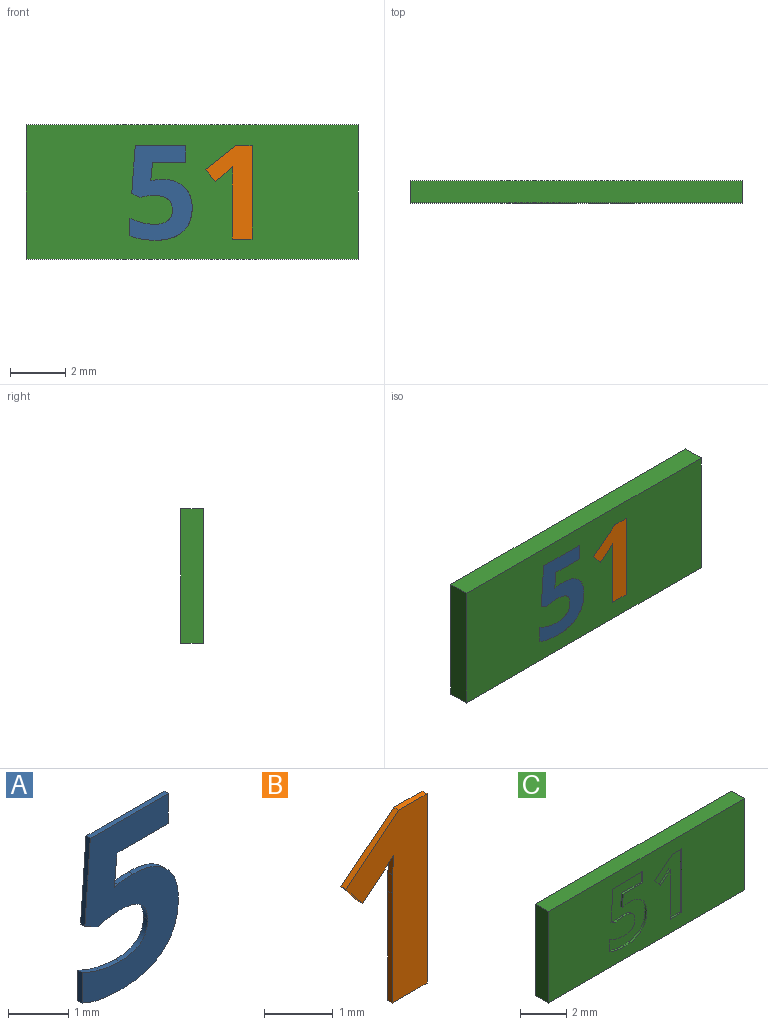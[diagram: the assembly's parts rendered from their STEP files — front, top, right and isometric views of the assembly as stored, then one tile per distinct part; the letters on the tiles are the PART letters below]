
ASSEMBLY  parts=3 mates=2
PART A: 22 faces, bbox 2.3x0.1x3.4 mm
  f0: plane 3.42x2.25mm, normal (0,-1,0), area 4.5mm2, adj f1,f2,f3,f4,f5,f6,f7,f8
  f1: plane 0.1x0.08mm, normal (-0.2,0,0.98), area 0mm2, adj f0,f2,f18,f20
  f2: plane 0.66x0.1mm, normal (1,0,-0.09), area 0.1mm2, adj f0,f1,f3,f18
  f3: plane 1.2x0.1mm, normal (0,0,-1), area 0.1mm2, adj f0,f2,f4,f18
  f4: plane 0.6x0.1mm, normal (1,0,0), area 0.1mm2, adj f0,f3,f5,f18
  f5: plane 1.83x0.1mm, normal (0,0,1), area 0.2mm2, adj f0,f4,f6,f18
  f6: plane 1.72x0.13mm, normal (-1,0,0.07), area 0.2mm2, adj f0,f5,f7,f18
  f7: plane 0.28x0.15mm, normal (-0.47,0,-0.88), area 0mm2, adj f0,f6,f8,f18
  f8: extruded ~0.24x0.1mm, area 0mm2, adj f0,f7,f9,f18
  f9: extruded ~0.27x0.1mm, area 0mm2, adj f0,f8,f10,f18
  f10: extruded ~0.68x0.51mm, area 0.1mm2, adj f0,f9,f11,f18
  f11: extruded ~0.65x0.54mm, area 0.1mm2, adj f0,f10,f12,f18
  f12: extruded ~0.46x0.1mm, area 0mm2, adj f0,f11,f13,f18
  f13: extruded ~0.42x0.16mm, area 0mm2, adj f0,f12,f14,f18
  f14: plane 0.62x0.1mm, normal (-1,0,0), area 0.1mm2, adj f0,f13,f15,f18
  f15: extruded ~0.91x0.18mm, area 0.1mm2, adj f0,f14,f16,f18
  f16: extruded ~1x0.3mm, area 0.1mm2, adj f0,f15,f17,f18
  f17: extruded ~0.87x0.35mm, area 0.1mm2, adj f0,f16,f18,f19
  f18: plane 3.42x2.25mm, normal (0,1,0), area 4.5mm2, adj f1,f2,f3,f4,f5,f6,f7,f8
  f19: extruded ~0.75x0.29mm, area 0.1mm2, adj f0,f17,f18,f21
  f20: extruded ~0.35x0.1mm, area 0mm2, adj f0,f1,f18,f21
  f21: extruded ~0.78x0.27mm, area 0.1mm2, adj f0,f18,f19,f20
PART B: 12 faces, bbox 1.7x0.1x3.4 mm
  f0: plane 3.37x1.67mm, normal (0,-1,0), area 2.9mm2, adj f1,f2,f3,f4,f5,f6,f7,f9
  f1: plane 0.59x0.1mm, normal (0,0,1), area 0.1mm2, adj f0,f2,f8,f10
  f2: plane 1.09x0.86mm, normal (-0.62,0,0.78), area 0.1mm2, adj f0,f1,f3,f8
  f3: plane 0.43x0.34mm, normal (-0.78,0,-0.63), area 0.1mm2, adj f0,f2,f4,f8
  f4: plane 0.39x0.31mm, normal (0.63,0,-0.78), area 0mm2, adj f0,f3,f5,f8
  f5: extruded ~0.25x0.23mm, area 0mm2, adj f0,f4,f6,f8
  f6: plane 0.35x0.1mm, normal (-1,0,0.03), area 0mm2, adj f0,f5,f7,f8
  f7: plane 0.32x0.1mm, normal (-1,0,0.02), area 0mm2, adj f0,f6,f8,f9
  f8: plane 3.37x1.67mm, normal (0,1,0), area 2.9mm2, adj f1,f2,f3,f4,f5,f6,f7,f9
  f9: plane 1.95x0.1mm, normal (-1,0,0), area 0.2mm2, adj f0,f7,f8,f11
  f10: plane 3.37x0.1mm, normal (1,0,0), area 0.3mm2, adj f0,f1,f8,f11
  f11: plane 0.71x0.1mm, normal (0,0,-1), area 0.1mm2, adj f0,f8,f9,f10
PART C: 38 faces, bbox 12x0.8x4.9 mm
  f0: plane 12x4.85mm, normal (0,-1,0), area 50.8mm2, adj f1,f2,f3,f4,f6,f7,f8,f9
  f1: plane 12x0.8mm, normal (0,0,-1), area 9.6mm2, adj f0,f2,f4,f5
  f2: plane 4.85x0.8mm, normal (1,0,0), area 3.9mm2, adj f0,f1,f3,f5
  f3: plane 12x0.8mm, normal (0,0,1), area 9.6mm2, adj f0,f2,f4,f5
  f4: plane 4.85x0.8mm, normal (-1,0,0), area 3.9mm2, adj f0,f1,f3,f5
  f5: plane 12x4.85mm, normal (0,1,0), area 58.2mm2, adj f1,f2,f3,f4
  f6: plane 3.37x0.1mm, normal (-1,0,0), area 0.3mm2, adj f0,f7,f15,f16
  f7: plane 0.59x0.1mm, normal (0,0,-1), area 0.1mm2, adj f0,f6,f8,f16
  f8: plane 1.09x0.86mm, normal (0.62,0,-0.78), area 0.1mm2, adj f0,f7,f9,f16
  f9: plane 0.43x0.34mm, normal (0.78,0,0.63), area 0.1mm2, adj f0,f8,f10,f16
  f10: plane 0.39x0.31mm, normal (-0.63,0,0.78), area 0mm2, adj f0,f9,f11,f16
  f11: extruded ~0.25x0.23mm, area 0mm2, adj f0,f10,f12,f16
  f12: plane 0.35x0.1mm, normal (1,0,-0.03), area 0mm2, adj f0,f11,f13,f16
  f13: plane 0.32x0.1mm, normal (1,0,-0.02), area 0mm2, adj f0,f12,f14,f16
  f14: plane 1.95x0.1mm, normal (1,0,0), area 0.2mm2, adj f0,f13,f15,f16
  f15: plane 0.71x0.1mm, normal (0,0,1), area 0.1mm2, adj f0,f6,f14,f16
  f16: plane 3.37x1.67mm, normal (0,-1,0), area 2.9mm2, adj f6,f7,f8,f9,f10,f11,f12,f13
  f17: extruded ~0.35x0.1mm, area 0mm2, adj f0,f18,f36,f37
  f18: plane 0.1x0.08mm, normal (0.2,0,-0.98), area 0mm2, adj f0,f17,f19,f37
  f19: plane 0.66x0.1mm, normal (-1,0,0.09), area 0.1mm2, adj f0,f18,f20,f37
  f20: plane 1.2x0.1mm, normal (0,0,1), area 0.1mm2, adj f0,f19,f21,f37
  f21: plane 0.6x0.1mm, normal (-1,0,0), area 0.1mm2, adj f0,f20,f22,f37
  f22: plane 1.83x0.1mm, normal (0,0,-1), area 0.2mm2, adj f0,f21,f23,f37
  f23: plane 1.72x0.13mm, normal (1,0,-0.07), area 0.2mm2, adj f0,f22,f24,f37
  f24: plane 0.28x0.15mm, normal (0.47,0,0.88), area 0mm2, adj f0,f23,f25,f37
  f25: extruded ~0.24x0.1mm, area 0mm2, adj f0,f24,f26,f37
  f26: extruded ~0.27x0.1mm, area 0mm2, adj f0,f25,f27,f37
  f27: extruded ~0.68x0.51mm, area 0.1mm2, adj f0,f26,f28,f37
  f28: extruded ~0.65x0.54mm, area 0.1mm2, adj f0,f27,f29,f37
  f29: extruded ~0.46x0.1mm, area 0mm2, adj f0,f28,f30,f37
  f30: extruded ~0.42x0.16mm, area 0mm2, adj f0,f29,f31,f37
  f31: plane 0.62x0.1mm, normal (1,0,0), area 0.1mm2, adj f0,f30,f32,f37
  f32: extruded ~0.91x0.18mm, area 0.1mm2, adj f0,f31,f33,f37
  f33: extruded ~1x0.3mm, area 0.1mm2, adj f0,f32,f34,f37
  f34: extruded ~0.87x0.35mm, area 0.1mm2, adj f0,f33,f35,f37
  f35: extruded ~0.75x0.29mm, area 0.1mm2, adj f0,f34,f36,f37
  f36: extruded ~0.78x0.27mm, area 0.1mm2, adj f0,f17,f35,f37
  f37: plane 3.42x2.25mm, normal (0,-1,0), area 4.5mm2, adj f17,f18,f19,f20,f21,f22,f23,f24
PLACE A t=(-2.66,0.36,-0.05)mm
PLACE B t=(-0.23,0.36,-0.05)mm
PLACE C t=(-0.01,0.36,-0.05)mm
MATE fastened B.f0 <-> C.f0  axis (0,-1,0) through (1.45,-0.44,-1.75)mm
MATE fastened A.f0 <-> C.f0  axis (0,-1,0) through (-2.25,-0.44,-1.62)mm
